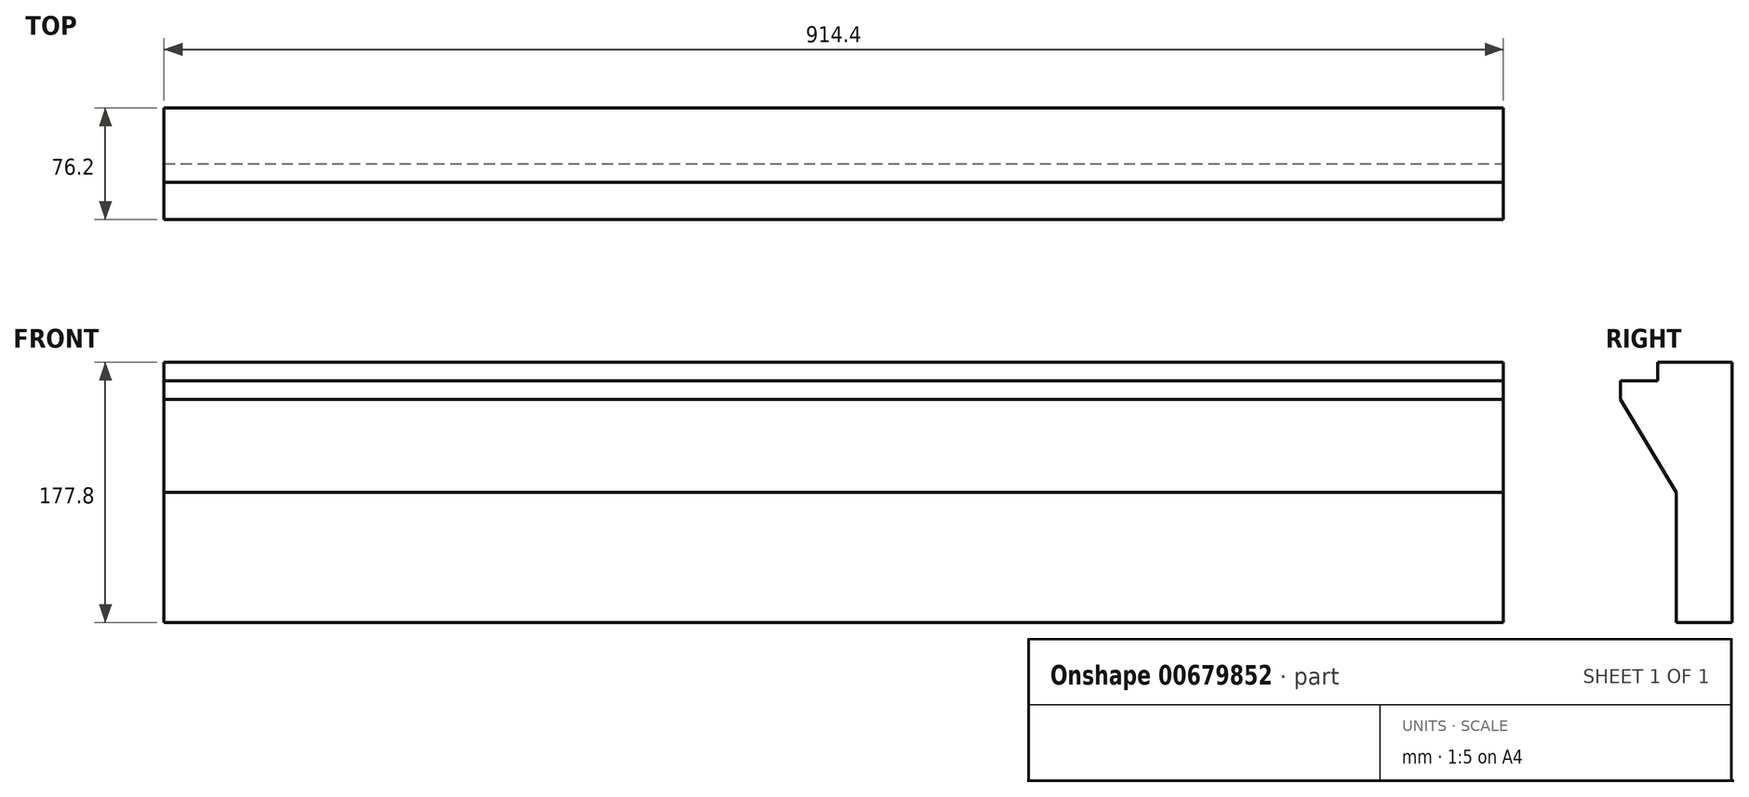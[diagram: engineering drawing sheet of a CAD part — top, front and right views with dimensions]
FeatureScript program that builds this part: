
annotation { "Feature Type Name" : "Feature", "Feature Type Description" : "" }
export const myFeature = defineFeature(function(context is Context, id is Id, definition is map)
    precondition{}
    {
        {
            var Q0;
            Q0=qCreatedBy(makeId("Top.planeOp"),FACE);
            var sketch = newSketch(context, id + "F0", { "sketchPlane" : qUnion([Q0])});
            skLineSegment(sketch, "E0.bottom", {"start": v(-131.9, 70.28) * mm, "end": v(782.5, 70.28) * mm});
            skLineSegment(sketch, "E0.top", {"start": v(-131.9, -5.92) * mm, "end": v(782.5, -5.92) * mm});
            skLineSegment(sketch, "E0.left", {"start": v(-131.9, 70.28) * mm, "end": v(-131.9, -5.92) * mm});
            skLineSegment(sketch, "E0.right", {"start": v(782.5, 70.28) * mm, "end": v(782.5, -5.92) * mm});
            skSolve(sketch);
        }
        {
            var Q0;
            Q0=makeQuery(id+"F0.imprint","IMPRINT",FACE,{"disambiguationData":[TD([[makeQuery(id+"F0.imprint","IMPRINT",EDGE,{"derivedFrom":sQuery(id+"F0.wireOp",EDGE,"E0.bottom")}),-1.0]])]});
            extrude(context, id + "F1", {"entities" : qUnion([Q0]), "depth" : 177.8 * mm, "offsetDistance" : 25.4 * mm});
        }
        {
            var Q0;
            Q0=makeQuery(id+"F1.opExtrude","SWEPT_FACE",FACE,{"disambiguationData":[OSD([sQuery(id+"F0.wireOp",EDGE,"E0.right")])]});
            var sketch = newSketch(context, id + "F2", { "sketchPlane" : qUnion([Q0])});
            skLineSegment(sketch, "E1", {"start": v(-5.92, 177.8) * mm, "end": v(-5.92, 152.4) * mm});
            skLineSegment(sketch, "E2", {"start": v(-5.92, 152.4) * mm, "end": v(32.18, 88.9) * mm});
            skLineSegment(sketch, "E3", {"start": v(32.18, 88.9) * mm, "end": v(32.18, 0) * mm});
            skSolve(sketch);
        }
        {
            var Q0;
            {var subQ0=sQuery(id+"F2.wireOp",EDGE,"E2");Q0=makeQuery(id+"F2.imprint","IMPRINT",FACE,{"disambiguationData":[TD([[makeQuery(id+"F2.imprint","IMPRINT",EDGE,{"derivedFrom":subQ0}),-1.0]])]});}
            extrude(context, id + "F3", {"entities" : qUnion([Q0]), "operationType" : NewBodyOperationType.REMOVE, "oppositeDirection" : true, "depth" : 2133.6 * mm, "offsetDistance" : 25.4 * mm});
        }
        {
            var Q0;
            Q0=makeQuery(id+"F1.opExtrude","SWEPT_FACE",FACE,{"disambiguationData":[OSD([sQuery(id+"F0.wireOp",EDGE,"E0.right")])]});
            var sketch = newSketch(context, id + "F4", { "sketchPlane" : qUnion([Q0])});
            skLineSegment(sketch, "E4", {"start": v(-5.92, 165.1) * mm, "end": v(19.48, 165.1) * mm});
            skLineSegment(sketch, "E5", {"start": v(19.48, 165.1) * mm, "end": v(19.48, 177.8) * mm});
            skSolve(sketch);
        }
        {
            var Q0;
            {var subQ0=sQuery(id+"F4.wireOp",EDGE,"E4");Q0=makeQuery(id+"F4.imprint","IMPRINT",FACE,{"disambiguationData":[TD([[makeQuery(id+"F4.imprint","IMPRINT",EDGE,{"derivedFrom":subQ0}),1.0]])]});}
            extrude(context, id + "F5", {"entities" : qUnion([Q0]), "operationType" : NewBodyOperationType.REMOVE, "oppositeDirection" : true, "depth" : 2438.4 * mm, "offsetDistance" : 25.4 * mm});
        }
    });
